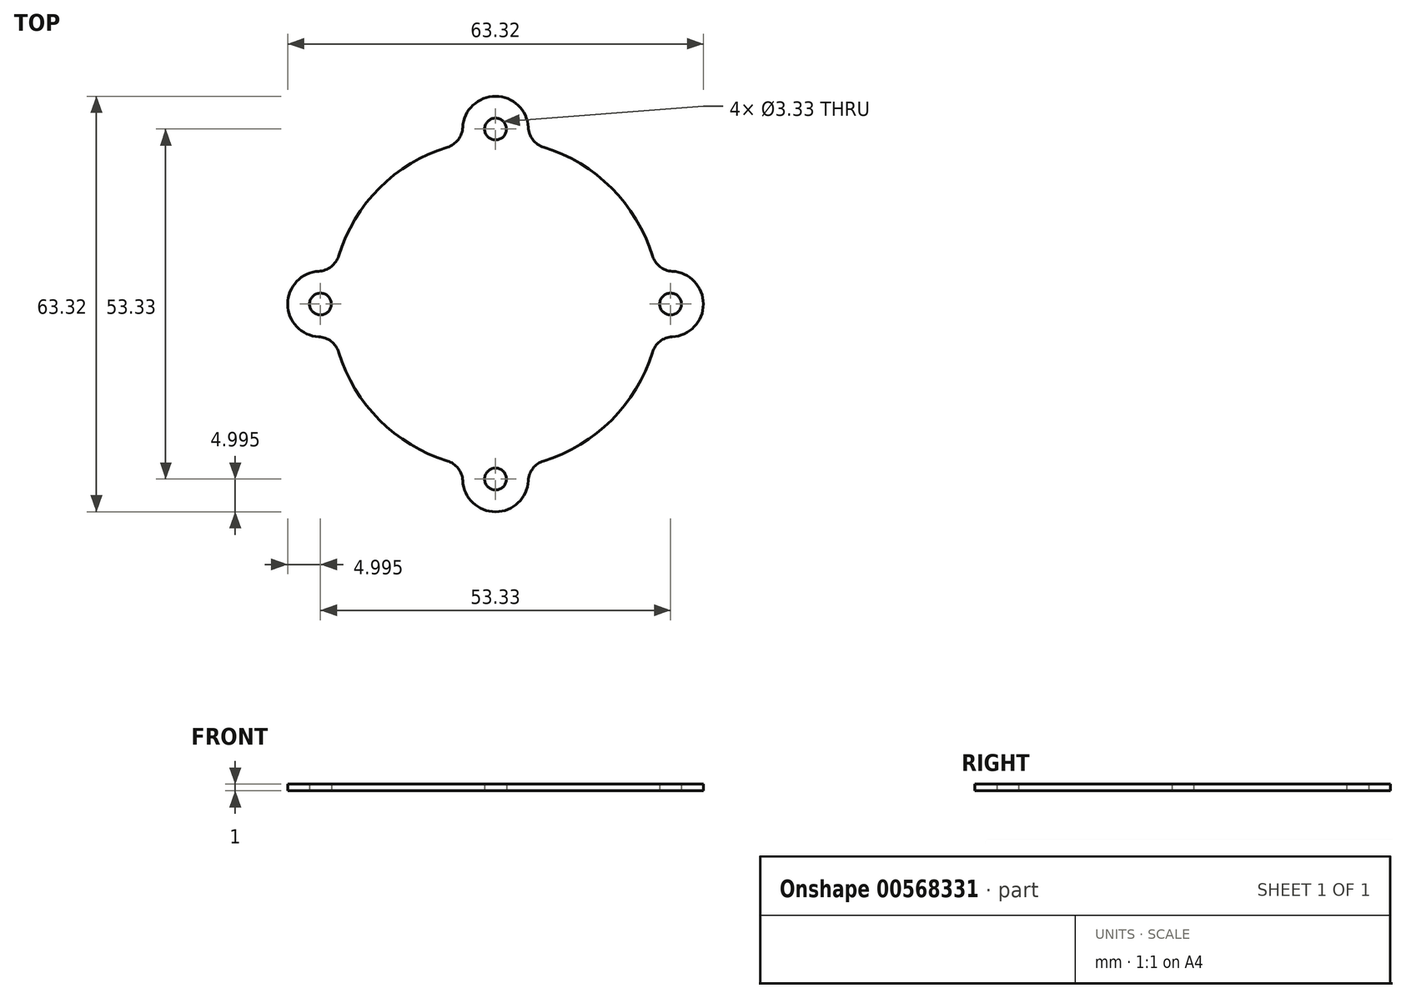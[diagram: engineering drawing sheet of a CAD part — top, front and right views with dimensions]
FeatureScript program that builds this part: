
annotation { "Feature Type Name" : "Feature", "Feature Type Description" : "" }
export const myFeature = defineFeature(function(context is Context, id is Id, definition is map)
    precondition{}
    {
        {
            assignVariable(context, id + "F0", {"name" : "p", "anyValue" : 3.33});
        }
        {
            assignVariable(context, id + "F1", {"name" : "tPBN", "anyValue" : 1});
        }
        {
            var Q0;
            Q0=qCreatedBy(makeId("Top.planeOp"),FACE);
            var sketch = newSketch(context, id + "F2", { "sketchPlane" : qUnion([Q0])});
            skCircle(sketch, "E0", {"center": v(0, 0) * mm, "radius": 25 * mm});
            skCircle(sketch, "E1", {"center": v(26.67, 0) * mm, "radius": 5 * mm});
            skCircle(sketch, "E2.1.0", {"center": v(0, -26.67) * mm, "radius": 5 * mm});
            skCircle(sketch, "E2.2.0", {"center": v(-26.67, 0) * mm, "radius": 5 * mm});
            skCircle(sketch, "E2.3.0", {"center": v(0, 26.67) * mm, "radius": 5 * mm});
            skLineSegment(sketch, "E2.anchor1", {"start": v(0, 0) * mm, "end": v(26.67, 0) * mm, "construction": true});
            skLineSegment(sketch, "E2.anchor2", {"start": v(0, 0) * mm, "end": v(0, 26.67) * mm, "construction": true});
            skCircle(sketch, "E3", {"center": v(0, 0) * mm, "radius": 26.67 * mm, "construction": true});
            skCircle(sketch, "E4", {"center": v(26.67, 0) * mm, "radius": 1.67 * mm});
            skCircle(sketch, "E5.1.0", {"center": v(0, 26.67) * mm, "radius": 1.67 * mm});
            skCircle(sketch, "E5.2.0", {"center": v(-26.67, 0) * mm, "radius": 1.67 * mm});
            skCircle(sketch, "E5.3.0", {"center": v(0, -26.67) * mm, "radius": 1.67 * mm});
            skSolve(sketch);
        }
        {
            var Q0;
            Q0 = qSketchRegion(id + "F2", true);
            extrude(context, id + "F3", {"entities" : qUnion([Q0]), "depth" : (getVariable(context, 'tPBN')) * mm, "offsetDistance" : 25 * mm});
        }
        {
            var Q0;
            {var subQ0=sQuery(id+"F2.wireOp",EDGE,"E1");var subQ1=sQuery(id+"F2.wireOp",EDGE,"E0");Q0=makeQuery(id+"F3.opExtrude","SWEPT_EDGE",EDGE,{"disambiguationData":[OSD([subQ1,subQ0]),TDD([makeQuery(id+"F2.imprint","INTERSECT",VERTEX,{"disambiguationData":[OD(1.0)],"derivedFrom":[subQ1,subQ0]})])]});}
            var Q1;
            {var subQ0=sQuery(id+"F2.wireOp",EDGE,"E2.1.0");var subQ1=sQuery(id+"F2.wireOp",EDGE,"E0");Q1=makeQuery(id+"F3.opExtrude","SWEPT_EDGE",EDGE,{"disambiguationData":[OSD([subQ1,subQ0]),TDD([makeQuery(id+"F2.imprint","INTERSECT",VERTEX,{"disambiguationData":[OD(1.0)],"derivedFrom":[subQ1,subQ0]})])]});}
            var Q2;
            {var subQ0=sQuery(id+"F2.wireOp",EDGE,"E2.1.0");var subQ1=sQuery(id+"F2.wireOp",EDGE,"E0");Q2=makeQuery(id+"F3.opExtrude","SWEPT_EDGE",EDGE,{"disambiguationData":[OSD([subQ1,subQ0]),TDD([makeQuery(id+"F2.imprint","INTERSECT",VERTEX,{"disambiguationData":[OD(0.0)],"derivedFrom":[subQ1,subQ0]})])]});}
            var Q3;
            {var subQ0=sQuery(id+"F2.wireOp",EDGE,"E2.2.0");var subQ1=sQuery(id+"F2.wireOp",EDGE,"E0");Q3=makeQuery(id+"F3.opExtrude","SWEPT_EDGE",EDGE,{"disambiguationData":[OSD([subQ1,subQ0]),TDD([makeQuery(id+"F2.imprint","INTERSECT",VERTEX,{"disambiguationData":[OD(1.0)],"derivedFrom":[subQ1,subQ0]})])]});}
            var Q4;
            {var subQ0=sQuery(id+"F2.wireOp",EDGE,"E2.2.0");var subQ1=sQuery(id+"F2.wireOp",EDGE,"E0");Q4=makeQuery(id+"F3.opExtrude","SWEPT_EDGE",EDGE,{"disambiguationData":[OSD([subQ1,subQ0]),TDD([makeQuery(id+"F2.imprint","INTERSECT",VERTEX,{"disambiguationData":[OD(0.0)],"derivedFrom":[subQ1,subQ0]})])]});}
            var Q5;
            {var subQ0=sQuery(id+"F2.wireOp",EDGE,"E2.3.0");var subQ1=sQuery(id+"F2.wireOp",EDGE,"E0");Q5=makeQuery(id+"F3.opExtrude","SWEPT_EDGE",EDGE,{"disambiguationData":[OSD([subQ1,subQ0]),TDD([makeQuery(id+"F2.imprint","INTERSECT",VERTEX,{"disambiguationData":[OD(1.0)],"derivedFrom":[subQ1,subQ0]})])]});}
            var Q6;
            {var subQ0=sQuery(id+"F2.wireOp",EDGE,"E2.3.0");var subQ1=sQuery(id+"F2.wireOp",EDGE,"E0");Q6=makeQuery(id+"F3.opExtrude","SWEPT_EDGE",EDGE,{"disambiguationData":[OSD([subQ1,subQ0]),TDD([makeQuery(id+"F2.imprint","INTERSECT",VERTEX,{"disambiguationData":[OD(0.0)],"derivedFrom":[subQ1,subQ0]})])]});}
            var Q7;
            {var subQ0=sQuery(id+"F2.wireOp",EDGE,"E1");var subQ1=sQuery(id+"F2.wireOp",EDGE,"E0");Q7=makeQuery(id+"F3.opExtrude","SWEPT_EDGE",EDGE,{"disambiguationData":[OSD([subQ1,subQ0]),TDD([makeQuery(id+"F2.imprint","INTERSECT",VERTEX,{"disambiguationData":[OD(0.0)],"derivedFrom":[subQ1,subQ0]})])]});}
            fillet(context, id + "F4", {"entities" : qUnion([Q0, Q1, Q2, Q3, Q4, Q5, Q6, Q7]), "radius" : (getVariable(context, 'p')) * mm, "tangentPropagation" : true, "allowEdgeOverflow" : false});
        }
    });
